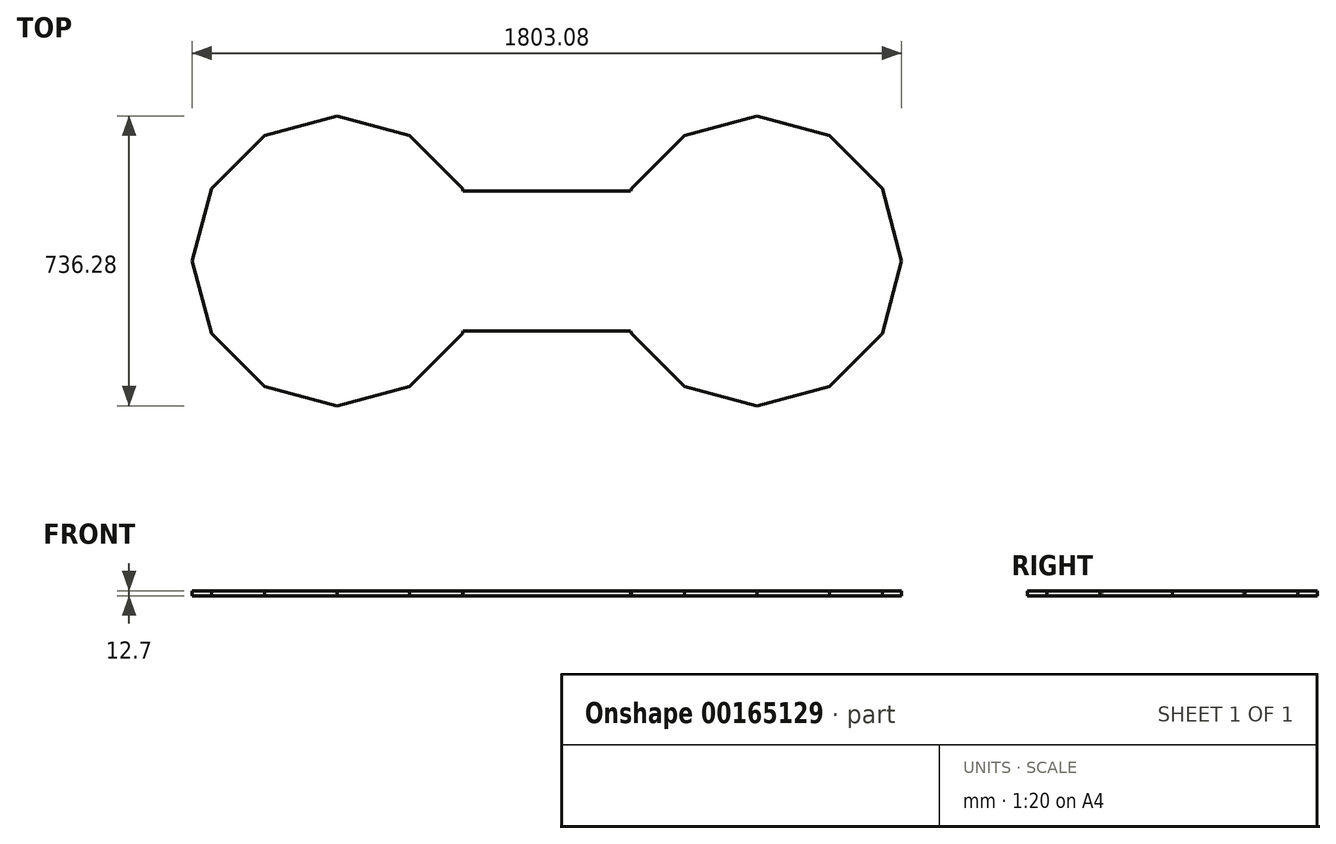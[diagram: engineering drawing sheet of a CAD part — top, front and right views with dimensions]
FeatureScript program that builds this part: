
annotation { "Feature Type Name" : "Feature", "Feature Type Description" : "" }
export const myFeature = defineFeature(function(context is Context, id is Id, definition is map)
    precondition{}
    {
        {
            var Q0;
            Q0=qCreatedBy(makeId("Top.planeOp"),FACE);
            var sketch = newSketch(context, id + "F0", { "sketchPlane" : qUnion([Q0])});
            skCircle(sketch, "E0.cCircle", {"center": v(0, 0) * mm, "radius": 355.6 * mm, "construction": true});
            skLineSegment(sketch, "E0.0", {"start": v(0, 368.14) * mm, "end": v(184.07, 318.82) * mm});
            skLineSegment(sketch, "E0.1", {"start": v(184.07, 318.82) * mm, "end": v(318.82, 184.07) * mm});
            skLineSegment(sketch, "E0.2", {"start": v(318.82, 184.07) * mm, "end": v(368.14, 0) * mm});
            skLineSegment(sketch, "E0.3", {"start": v(368.14, 0) * mm, "end": v(318.82, -184.07) * mm});
            skLineSegment(sketch, "E0.4", {"start": v(318.82, -184.07) * mm, "end": v(184.07, -318.82) * mm});
            skLineSegment(sketch, "E0.5", {"start": v(184.07, -318.82) * mm, "end": v(0, -368.14) * mm});
            skLineSegment(sketch, "E0.6", {"start": v(0, -368.14) * mm, "end": v(-184.07, -318.82) * mm});
            skLineSegment(sketch, "E0.7", {"start": v(-184.07, -318.82) * mm, "end": v(-318.82, -184.07) * mm});
            skLineSegment(sketch, "E0.8", {"start": v(-318.82, -184.07) * mm, "end": v(-368.14, 0) * mm});
            skLineSegment(sketch, "E0.9", {"start": v(-368.14, 0) * mm, "end": v(-318.82, 184.07) * mm});
            skLineSegment(sketch, "E0.10", {"start": v(-318.82, 184.07) * mm, "end": v(-184.07, 318.82) * mm});
            skLineSegment(sketch, "E0.11", {"start": v(-184.07, 318.82) * mm, "end": v(0, 368.14) * mm});
            skPoint(sketch, "E0.0.midPoint", {"position": v(92.04, 343.48) * mm});
            skLineSegment(sketch, "E1", {"start": v(0, 0) * mm, "end": v(0, 368.14) * mm, "construction": true});
            skSolve(sketch);
        }
        {
            var Q0;
            Q0=makeQuery(id+"F0.imprint","IMPRINT",FACE,{"disambiguationData":[TD([[makeQuery(id+"F0.imprint","IMPRINT",EDGE,{"derivedFrom":sQuery(id+"F0.wireOp",EDGE,"E0.0")}),-1.0]])]});
            extrude(context, id + "F1", {"entities" : qUnion([Q0]), "depth" : 12.7 * mm});
        }
        {
            var Q0;
            Q0=makeQuery(id+"F1.opExtrude","SWEPT_BODY",BODY,{"disambiguationData":[OSD([sQuery(id+"F0.wireOp",EDGE,"E0.0"),sQuery(id+"F0.wireOp",EDGE,"E0.1"),sQuery(id+"F0.wireOp",EDGE,"E0.2"),sQuery(id+"F0.wireOp",EDGE,"E0.3"),sQuery(id+"F0.wireOp",EDGE,"E0.4"),sQuery(id+"F0.wireOp",EDGE,"E0.5"),sQuery(id+"F0.wireOp",EDGE,"E0.6"),sQuery(id+"F0.wireOp",EDGE,"E0.7"),sQuery(id+"F0.wireOp",EDGE,"E0.8"),sQuery(id+"F0.wireOp",EDGE,"E0.9"),sQuery(id+"F0.wireOp",EDGE,"E0.10"),sQuery(id+"F0.wireOp",EDGE,"E0.11")])]});
            transform(context, id + "F2", {"entities" : qUnion([Q0]), "transformType" : TransformType.TRANSLATION_3D, "dx" : 1066.8 * mm, "dy" : 0 * mm, "dz" : 0 * mm, "makeCopy" : true});
        }
        {
            var Q0;
            Q0=makeQuery(id+"F2.opPattern","COPY",FACE,{"derivedFrom":makeQuery(id+"F1.opExtrude","CAP_FACE",FACE,{"disambiguationData":[OSD([sQuery(id+"F0.wireOp",EDGE,"E0.0"),sQuery(id+"F0.wireOp",EDGE,"E0.1"),sQuery(id+"F0.wireOp",EDGE,"E0.2"),sQuery(id+"F0.wireOp",EDGE,"E0.3"),sQuery(id+"F0.wireOp",EDGE,"E0.4"),sQuery(id+"F0.wireOp",EDGE,"E0.5"),sQuery(id+"F0.wireOp",EDGE,"E0.6"),sQuery(id+"F0.wireOp",EDGE,"E0.7"),sQuery(id+"F0.wireOp",EDGE,"E0.8"),sQuery(id+"F0.wireOp",EDGE,"E0.9"),sQuery(id+"F0.wireOp",EDGE,"E0.10"),sQuery(id+"F0.wireOp",EDGE,"E0.11")])],"isStart":false}),"instanceName":"1"});
            var sketch = newSketch(context, id + "F3", { "sketchPlane" : qUnion([Q0])});
            skLineSegment(sketch, "E2", {"start": v(-368.14, 0) * mm, "end": v(0, 0) * mm, "construction": true});
            skLineSegment(sketch, "E3", {"start": v(0, 0) * mm, "end": v(368.14, 0) * mm, "construction": true});
            skLineSegment(sketch, "E4", {"start": v(1434.94, 0) * mm, "end": v(1066.8, 0) * mm, "construction": true});
            skLineSegment(sketch, "E5", {"start": v(1066.8, 0) * mm, "end": v(698.66, 0) * mm, "construction": true});
            skLineSegment(sketch, "E6.bottom", {"start": v(0, 177.8) * mm, "end": v(1066.8, 177.8) * mm});
            skLineSegment(sketch, "E6.top", {"start": v(0, -177.8) * mm, "end": v(1066.8, -177.8) * mm});
            skLineSegment(sketch, "E6.left", {"start": v(0, 177.8) * mm, "end": v(0, -177.8) * mm});
            skLineSegment(sketch, "E6.right", {"start": v(1066.8, 177.8) * mm, "end": v(1066.8, -177.8) * mm});
            skSolve(sketch);
        }
        {
            var Q0;
            Q0 = qSketchRegion(id + "F3", true);
            var Q1;
            Q1=makeQuery(id+"F1.opExtrude","CAP_FACE",FACE,{"disambiguationData":[OSD([sQuery(id+"F0.wireOp",EDGE,"E0.0"),sQuery(id+"F0.wireOp",EDGE,"E0.1"),sQuery(id+"F0.wireOp",EDGE,"E0.2"),sQuery(id+"F0.wireOp",EDGE,"E0.3"),sQuery(id+"F0.wireOp",EDGE,"E0.4"),sQuery(id+"F0.wireOp",EDGE,"E0.5"),sQuery(id+"F0.wireOp",EDGE,"E0.6"),sQuery(id+"F0.wireOp",EDGE,"E0.7"),sQuery(id+"F0.wireOp",EDGE,"E0.8"),sQuery(id+"F0.wireOp",EDGE,"E0.9"),sQuery(id+"F0.wireOp",EDGE,"E0.10"),sQuery(id+"F0.wireOp",EDGE,"E0.11")])],"isStart":true});
            extrude(context, id + "F4", {"entities" : qUnion([Q0]), "operationType" : NewBodyOperationType.ADD, "endBound" : BoundingType.UP_TO_SURFACE, "oppositeDirection" : true, "endBoundEntityFace" : qUnion([Q1]), "depth" : 25.4 * mm});
        }
    });
